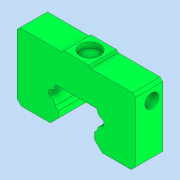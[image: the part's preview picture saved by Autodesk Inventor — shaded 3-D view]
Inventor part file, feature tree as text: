
AUTODESK INVENTOR PART (.ipt)
format: ipt  version: 2021 (Build 250183000, 183)  size: 159,744 bytes
history: native  units: mm
features: extrude x3, sketch x3, projected_geometry x2, mirror x1
ambient origin geometry x8: Origin, YZ Plane, XZ Plane, XY Plane, X Axis, Y Axis, Z Axis, Center Point
bodies: Solid1 (feature_tree)
feature tree (9):
  extrude  "Extrusion1"  Depth=6.7mm TaperAngle=0.0deg
  extrude  "Extrusion2"  [1 undecoded]
  mirror  "Mirror1"
  extrude  "Extrusion3"  [1 undecoded]
  sketch  "Sketch1"  dims[d0=10.0mm d1=0.0mm d2=6.7mm d3=0.0mm]
  sketch  "Sketch2"  dims[d4=2.0mm d5=0.0mm]
  projected_geometry  "Projected Loop1"
  sketch  "Sketch3"
  projected_geometry  "Projected Loop2"
note: 2 required parameter values undecoded (feature->parameter linkage not recoverable at this tier; creation-order binding heuristic only, values carry confidence <= 0.55)
